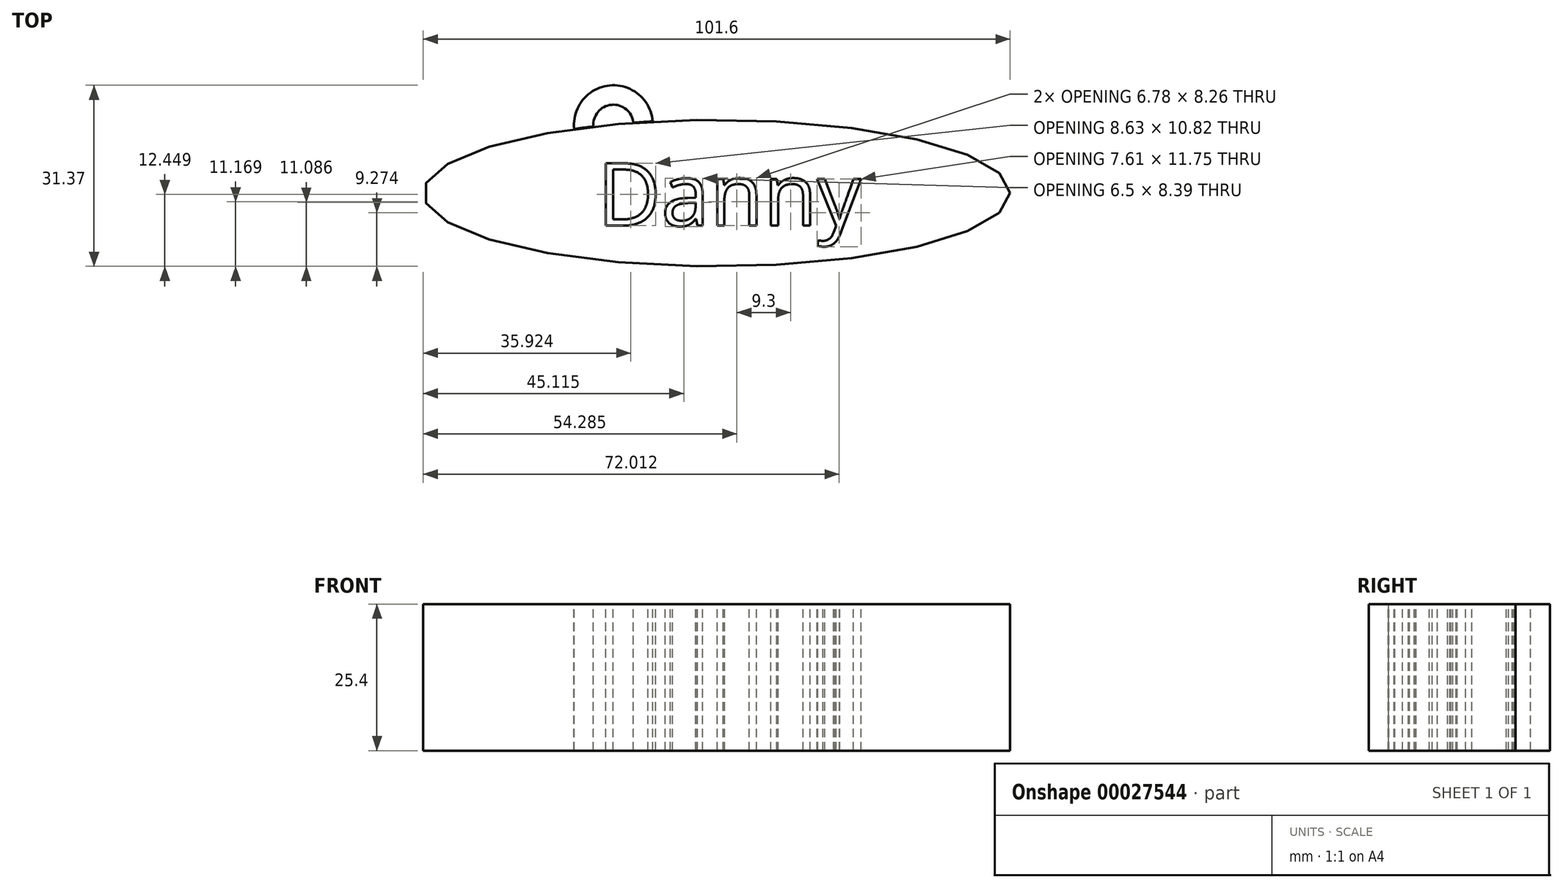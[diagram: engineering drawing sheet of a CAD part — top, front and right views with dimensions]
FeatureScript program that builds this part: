
annotation { "Feature Type Name" : "Feature", "Feature Type Description" : "" }
export const myFeature = defineFeature(function(context is Context, id is Id, definition is map)
    precondition{}
    {
        {
            var Q0;
            Q0=qCreatedBy(makeId("Top.planeOp"),FACE);
            var sketch = newSketch(context, id + "F0", { "sketchPlane" : qUnion([Q0])});
            skEllipse(sketch, "E0", {"center": v(-23.6, 14.23) * mm, "majorRadius": 50.8 * mm, "minorRadius": 12.7 * mm, "majorAxis": v(1, 0)});
            skSolve(sketch);
        }
        {
            var Q0;
            Q0=makeQuery(id+"F0.imprint","IMPRINT",FACE,{"disambiguationData":[TD([[makeQuery(id+"F0.imprint","IMPRINT",EDGE,{"derivedFrom":sQuery(id+"F0.wireOp",EDGE,"E0")}),1.0]])]});
            var sketch = newSketch(context, id + "F1", { "sketchPlane" : qUnion([Q0])});
            skCircle(sketch, "E1", {"center": v(-41.48, 26.06) * mm, "radius": 6.84 * mm});
            skCircle(sketch, "E2", {"center": v(-41.48, 26.06) * mm, "radius": 3.47 * mm});
            skSolve(sketch);
        }
        {
            var Q0;
            Q0=makeQuery(id+"F0.imprint","IMPRINT",FACE,{"disambiguationData":[TD([[makeQuery(id+"F0.imprint","IMPRINT",EDGE,{"derivedFrom":sQuery(id+"F0.wireOp",EDGE,"E0")}),1.0]])]});
            var Q1;
            {var subQ0=makeQuery(id+"F0.imprint","IMPRINT",EDGE,{"derivedFrom":sQuery(id+"F0.wireOp",EDGE,"E0")});var subQ3=sQuery(id+"F1.wireOp",EDGE,"E1");var subQ4=makeQuery(id+"F1.imprint","INTERSECT",VERTEX,{"disambiguationData":[OD(0.0)],"derivedFrom":[subQ0,subQ3]});Q1=makeQuery(id+"F1.imprint","IMPRINT",FACE,{"disambiguationData":[TD([[makeQuery(id+"F1.imprint","IMPRINT",EDGE,{"disambiguationData":[TD([[subQ4,1.0]])],"derivedFrom":subQ3}),1.0]])]});}
            extrude(context, id + "F2", {"entities" : qUnion([Q0, Q1]), "oppositeDirection" : true, "depth" : 25.4 * mm});
        }
        {
            var Q0;
            Q0=makeQuery(id+"F2.opExtrude","CAP_FACE",FACE,{"disambiguationData":[OSD([sQuery(id+"F0.wireOp",EDGE,"E0")])],"isStart":true});
            var sketch = newSketch(context, id + "F3", { "sketchPlane" : qUnion([Q0])});
            skText(sketch, "E3", { "text": "Danny", "fontName": "OpenSans-Regular.ttf"});
            const initialGuessF3  = {"E3": [-0.04428, 0.00857, 1, 0, 0.01091]};
            skSetInitialGuess(sketch, initialGuessF3);
            skSolve(sketch);
        }
        {
            var Q0;
            Q0 = qSketchRegion(id + "F3", true);
            var Q1;
            Q1=makeQuery(id+"F2.opExtrude","CAP_FACE",FACE,{"disambiguationData":[OSD([sQuery(id+"F0.wireOp",EDGE,"E0")])],"isStart":false});
            extrude(context, id + "F4", {"entities" : qUnion([Q0]), "operationType" : NewBodyOperationType.REMOVE, "endBound" : BoundingType.UP_TO_SURFACE, "oppositeDirection" : true, "endBoundEntityFace" : qUnion([Q1]), "depth" : 37.44 * mm});
        }
    });
